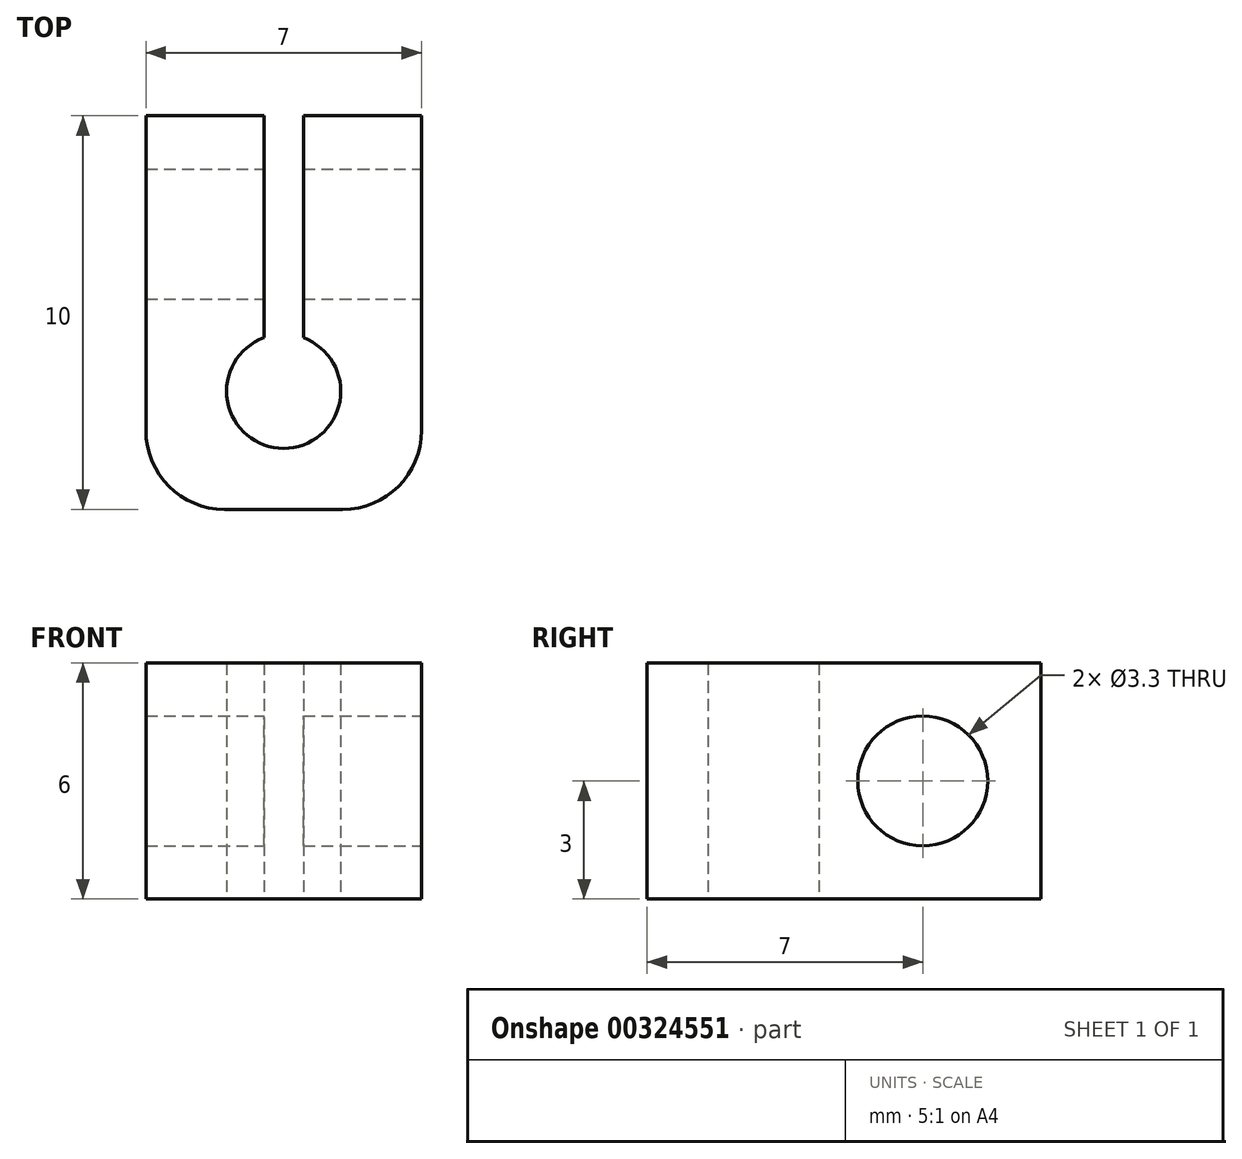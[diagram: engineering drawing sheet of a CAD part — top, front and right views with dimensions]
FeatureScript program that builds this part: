
annotation { "Feature Type Name" : "Feature", "Feature Type Description" : "" }
export const myFeature = defineFeature(function(context is Context, id is Id, definition is map)
    precondition{}
    {
        {
            var Q0;
            Q0=qCreatedBy(makeId("Top.planeOp"),FACE);
            var sketch = newSketch(context, id + "F0", { "sketchPlane" : qUnion([Q0])});
            skLineSegment(sketch, "E0.bottom", {"start": v(-3.5, 7) * mm, "end": v(3.5, 7) * mm});
            skLineSegment(sketch, "E0.top", {"start": v(-3.5, -3) * mm, "end": v(3.5, -3) * mm});
            skLineSegment(sketch, "E0.left", {"start": v(-3.5, 7) * mm, "end": v(-3.5, -3) * mm});
            skLineSegment(sketch, "E0.right", {"start": v(3.5, 7) * mm, "end": v(3.5, -3) * mm});
            skCircle(sketch, "E1", {"center": v(0, 0) * mm, "radius": 1.45 * mm});
            skLineSegment(sketch, "E2", {"start": v(0, 7) * mm, "end": v(0, -3) * mm, "construction": true});
            skLineSegment(sketch, "E3.bottom", {"start": v(-0.5, 7) * mm, "end": v(0.5, 7) * mm});
            skLineSegment(sketch, "E3.top", {"start": v(-0.5, 1.36) * mm, "end": v(0.5, 1.36) * mm});
            skLineSegment(sketch, "E3.left", {"start": v(-0.5, 7) * mm, "end": v(-0.5, 1.36) * mm});
            skLineSegment(sketch, "E3.right", {"start": v(0.5, 7) * mm, "end": v(0.5, 1.36) * mm});
            skSolve(sketch);
        }
        {
            var Q0;
            Q0=makeQuery(id+"F0.imprint","IMPRINT",FACE,{"disambiguationData":[TD([[makeQuery(id+"F0.imprint","IMPRINT",EDGE,{"derivedFrom":sQuery(id+"F0.wireOp",EDGE,"E0.top")}),1.0]])]});
            extrude(context, id + "F1", {"entities" : qUnion([Q0]), "depth" : 6 * mm});
        }
        {
            var Q0;
            Q0=makeQuery(id+"F1.opExtrude","SWEPT_FACE",FACE,{"disambiguationData":[OSD([sQuery(id+"F0.wireOp",EDGE,"E0.right")])]});
            var sketch = newSketch(context, id + "F2", { "sketchPlane" : qUnion([Q0])});
            skCircle(sketch, "E4", {"center": v(4, 3) * mm, "radius": 1.65 * mm});
            skSolve(sketch);
        }
        {
            var Q0;
            Q0=makeQuery(id+"F2.imprint","IMPRINT",FACE,{"disambiguationData":[TD([[makeQuery(id+"F2.imprint","IMPRINT",EDGE,{"derivedFrom":sQuery(id+"F2.wireOp",EDGE,"E4")}),1.0]])]});
            extrude(context, id + "F3", {"entities" : qUnion([Q0]), "operationType" : NewBodyOperationType.REMOVE, "oppositeDirection" : true, "depth" : 25 * mm});
        }
        {
            var Q0;
            Q0=makeQuery(id+"F1.opExtrude","SWEPT_EDGE",EDGE,{"disambiguationData":[OSD([sQuery(id+"F0.wireOp",EDGE,"E0.top"),sQuery(id+"F0.wireOp",EDGE,"E0.right")])]});
            var Q1;
            Q1=makeQuery(id+"F1.opExtrude","SWEPT_EDGE",EDGE,{"disambiguationData":[OSD([sQuery(id+"F0.wireOp",EDGE,"E0.top"),sQuery(id+"F0.wireOp",EDGE,"E0.left")])]});
            fillet(context, id + "F4", {"entities" : qUnion([Q0, Q1]), "radius" : 2 * mm, "tangentPropagation" : true, "allowEdgeOverflow" : false});
        }
    });
